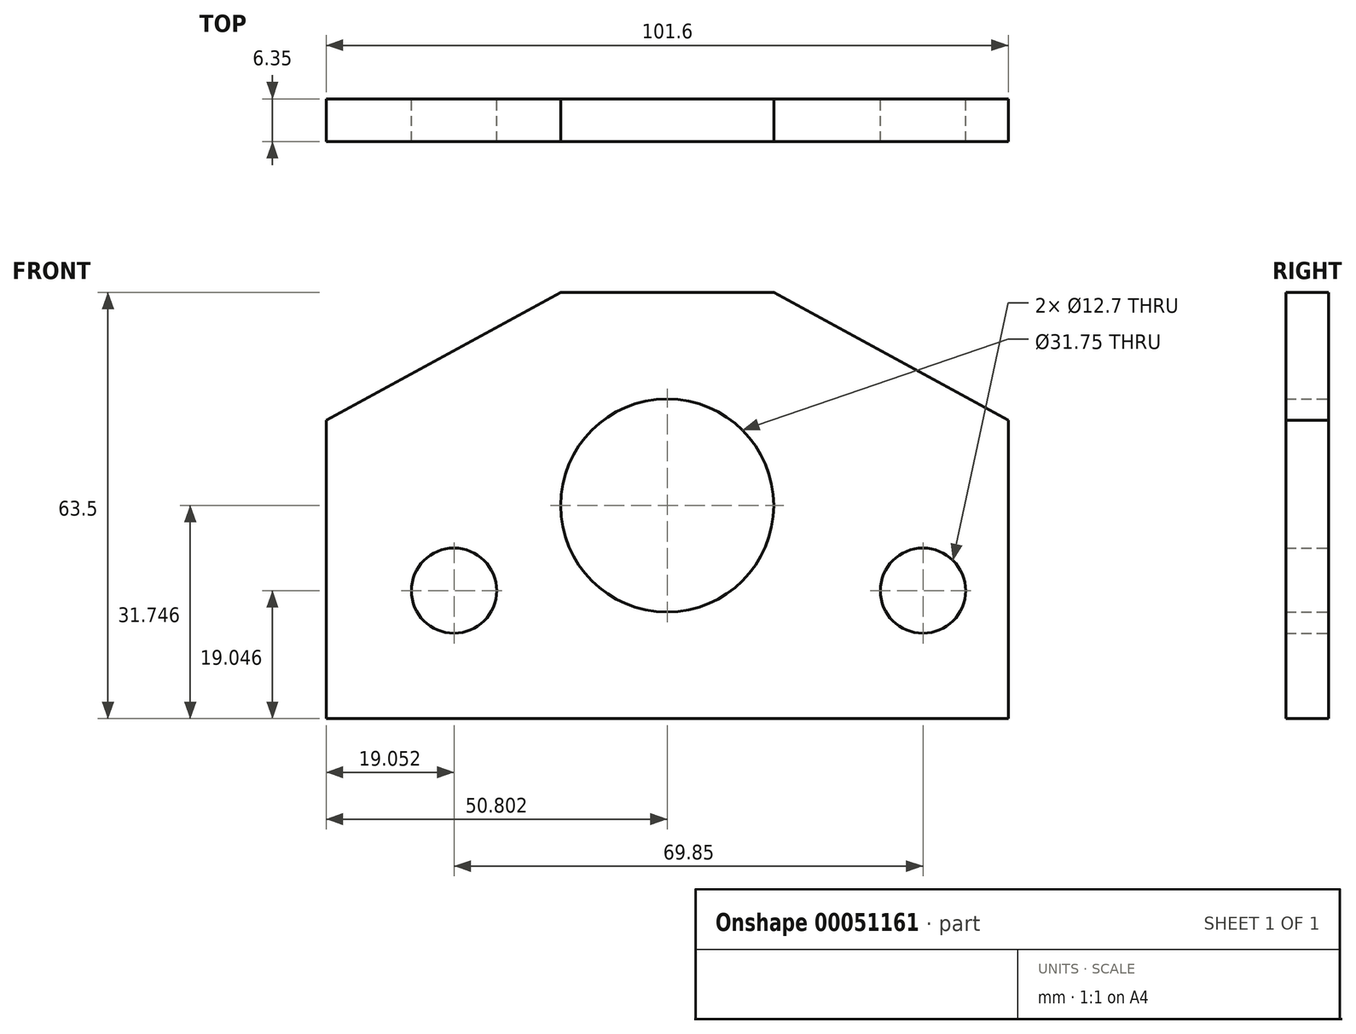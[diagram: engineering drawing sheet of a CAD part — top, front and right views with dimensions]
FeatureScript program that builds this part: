
annotation { "Feature Type Name" : "Feature", "Feature Type Description" : "" }
export const myFeature = defineFeature(function(context is Context, id is Id, definition is map)
    precondition{}
    {
        {
            var Q0;
            Q0=qCreatedBy(makeId("Front.planeOp"),FACE);
            var sketch = newSketch(context, id + "F0", { "sketchPlane" : qUnion([Q0])});
            skLineSegment(sketch, "E0.bottom", {"start": v(-30.75, 50.45) * mm, "end": v(1, 50.45) * mm});
            skLineSegment(sketch, "E0.top", {"start": v(-65.68, -13.05) * mm, "end": v(35.92, -13.05) * mm});
            skLineSegment(sketch, "E0.left", {"start": v(-65.68, 31.4) * mm, "end": v(-65.68, -13.05) * mm});
            skLineSegment(sketch, "E0.right", {"start": v(35.92, 31.4) * mm, "end": v(35.92, -13.05) * mm});
            skPoint(sketch, "E1", {"position": v(35.92, 31.4) * mm});
            skPoint(sketch, "E2", {"position": v(-14.88, 50.45) * mm});
            skLineSegment(sketch, "E3", {"start": v(1, 50.45) * mm, "end": v(35.92, 31.4) * mm});
            skLineSegment(sketch, "E4", {"start": v(-30.75, 50.45) * mm, "end": v(-65.68, 31.4) * mm});
            skPoint(sketch, "E5.orphan", {"position": v(-65.68, 50.45) * mm});
            skPoint(sketch, "E6.orphan", {"position": v(35.92, 50.45) * mm});
            skCircle(sketch, "E7", {"center": v(-46.63, 6) * mm, "radius": 6.35 * mm});
            skCircle(sketch, "E8", {"center": v(23.22, 6) * mm, "radius": 6.35 * mm});
            skCircle(sketch, "E9", {"center": v(-14.88, 18.7) * mm, "radius": 15.88 * mm});
            skLineSegment(sketch, "E10", {"start": v(-14.88, 50.45) * mm, "end": v(-14.88, -13.05) * mm, "construction": true});
            skSolve(sketch);
        }
        {
            var Q0;
            Q0 = qSketchRegion(id + "F0", true);
            extrude(context, id + "F1", {"entities" : qUnion([Q0]), "depth" : 6.35 * mm});
        }
    });
